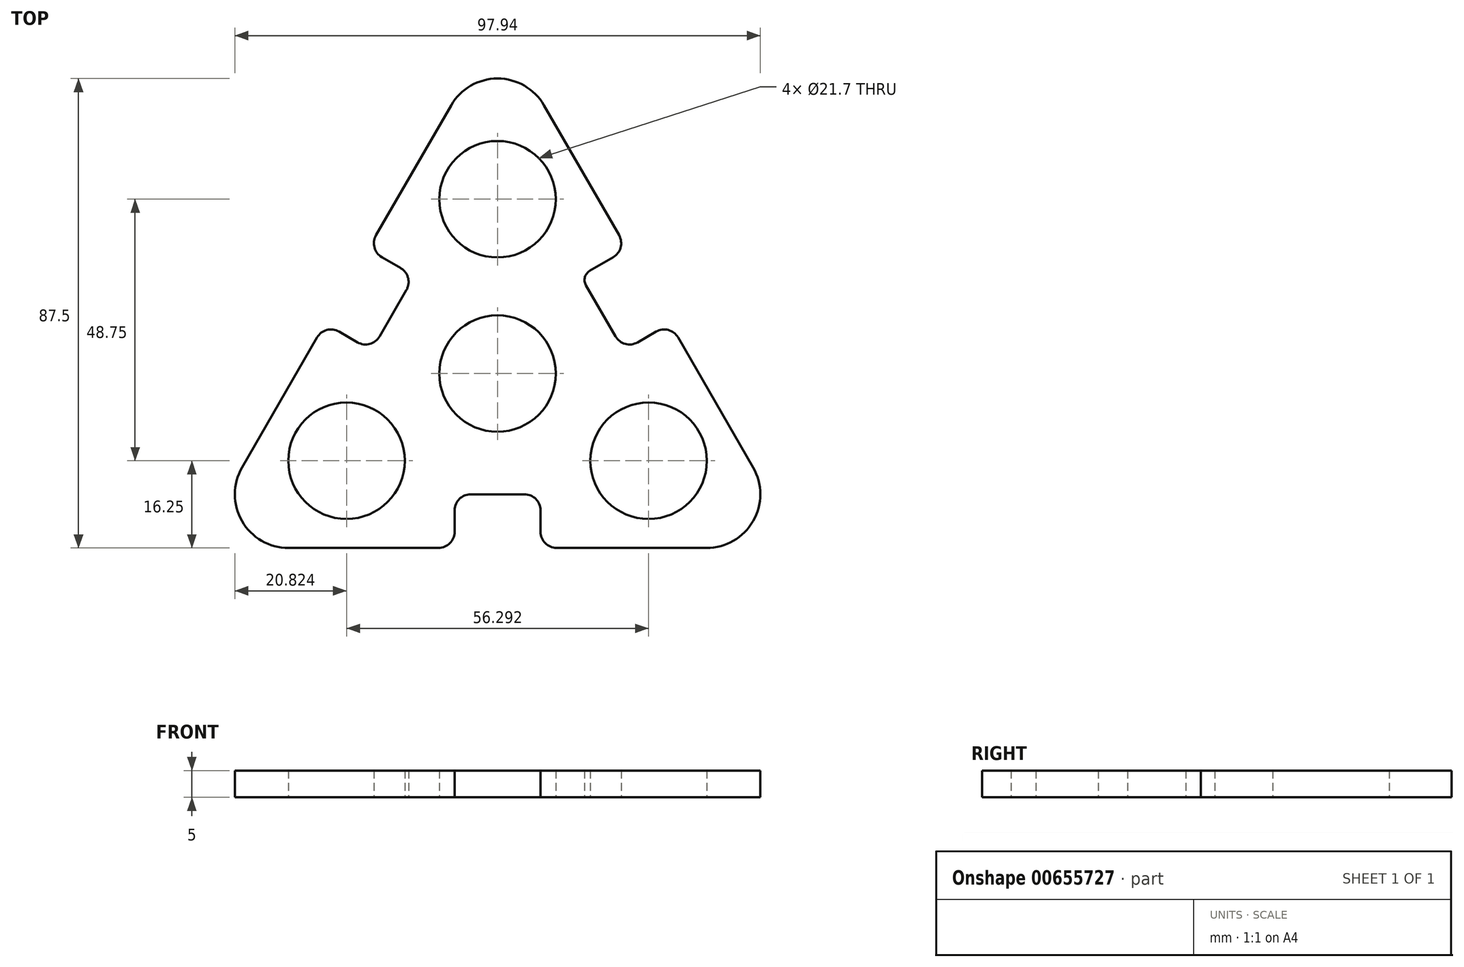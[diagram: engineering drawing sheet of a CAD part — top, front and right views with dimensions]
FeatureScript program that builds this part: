
annotation { "Feature Type Name" : "Feature", "Feature Type Description" : "" }
export const myFeature = defineFeature(function(context is Context, id is Id, definition is map)
    precondition{}
    {
        {
            var Q0;
            Q0=qCreatedBy(makeId("Top.planeOp"),FACE);
            var sketch = newSketch(context, id + "F0", { "sketchPlane" : qUnion([Q0])});
            skCircle(sketch, "E0.cCircle", {"center": v(0, 0) * mm, "radius": 32.5 * mm, "construction": true});
            skLineSegment(sketch, "E0.0", {"start": v(42.44, -32.5) * mm, "end": v(11, -32.5) * mm});
            skLineSegment(sketch, "E0.1", {"start": v(-56.3, -32.5) * mm, "end": v(0, 65) * mm, "construction": true});
            skLineSegment(sketch, "E0.2", {"start": v(0, 65) * mm, "end": v(56.3, -32.5) * mm, "construction": true});
            skPoint(sketch, "E0.0.midPoint", {"position": v(0, -32.5) * mm});
            skLineSegment(sketch, "E1.bottom", {"start": v(5, -22.5) * mm, "end": v(-5, -22.5) * mm});
            skLineSegment(sketch, "E1.left", {"start": v(8, -25.5) * mm, "end": v(8, -29.5) * mm});
            skLineSegment(sketch, "E1.right", {"start": v(-8, -25.5) * mm, "end": v(-8, -29.5) * mm});
            skLineSegment(sketch, "E2.trimOffspring", {"start": v(-11, -32.5) * mm, "end": v(-21.64, -32.5) * mm});
            skLineSegment(sketch, "E3", {"start": v(0, 0) * mm, "end": v(-28.15, -16.25) * mm, "construction": true});
            skCircle(sketch, "E4", {"center": v(-28.15, -16.25) * mm, "radius": 10.85 * mm});
            skCircle(sketch, "E5.1.0", {"center": v(28.15, -16.25) * mm, "radius": 10.85 * mm});
            skLineSegment(sketch, "E5.1.1", {"start": v(26.08, 5.82) * mm, "end": v(29.55, 7.82) * mm});
            skLineSegment(sketch, "E5.1.2", {"start": v(16.49, 16.45) * mm, "end": v(21.99, 6.92) * mm});
            skLineSegment(sketch, "E5.1.3", {"start": v(17.22, 19.18) * mm, "end": v(21.55, 21.68) * mm});
            skCircle(sketch, "E5.2.0", {"center": v(0, 32.5) * mm, "radius": 10.85 * mm});
            skLineSegment(sketch, "E5.2.1", {"start": v(-18.08, 19.68) * mm, "end": v(-21.55, 21.68) * mm});
            skLineSegment(sketch, "E5.2.2", {"start": v(-21.99, 6.92) * mm, "end": v(-16.99, 15.58) * mm});
            skLineSegment(sketch, "E5.2.3", {"start": v(-26.08, 5.82) * mm, "end": v(-29.55, 7.82) * mm});
            skLineSegment(sketch, "E6", {"start": v(22.65, 25.78) * mm, "end": v(4.76, 56.75) * mm});
            skLineSegment(sketch, "E7", {"start": v(-4.76, 56.75) * mm, "end": v(-22.65, 25.78) * mm});
            skLineSegment(sketch, "E8", {"start": v(-33.65, 6.72) * mm, "end": v(-51.53, -24.25) * mm});
            skLineSegment(sketch, "E9", {"start": v(51.53, -24.25) * mm, "end": v(33.65, 6.72) * mm});
            skPoint(sketch, "E10.visualSharp", {"position": v(-8, -32.5) * mm});
            skArc(sketch, "E10.filletArc", {"start": v(-11, -32.5) * mm, "mid": v(-8.88, -31.62) * mm, "end": v(-8, -29.5) * mm});
            skPoint(sketch, "E11.visualSharp", {"position": v(8, -32.5) * mm});
            skArc(sketch, "E11.filletArc", {"start": v(8, -29.5) * mm, "mid": v(8.88, -31.62) * mm, "end": v(11, -32.5) * mm});
            skPoint(sketch, "E12.visualSharp", {"position": v(-32.15, 9.32) * mm});
            skArc(sketch, "E12.filletArc", {"start": v(-29.55, 7.82) * mm, "mid": v(-31.82, 8.12) * mm, "end": v(-33.65, 6.72) * mm});
            skPoint(sketch, "E13.visualSharp", {"position": v(-24.15, 23.18) * mm});
            skArc(sketch, "E13.filletArc", {"start": v(-22.65, 25.78) * mm, "mid": v(-22.95, 23.5) * mm, "end": v(-21.55, 21.68) * mm});
            skPoint(sketch, "E14.visualSharp", {"position": v(-15.49, 18.18) * mm});
            skArc(sketch, "E14.filletArc", {"start": v(-16.99, 15.58) * mm, "mid": v(-16.69, 17.86) * mm, "end": v(-18.08, 19.68) * mm});
            skPoint(sketch, "E15.visualSharp", {"position": v(-23.49, 4.32) * mm});
            skArc(sketch, "E15.filletArc", {"start": v(-26.08, 5.82) * mm, "mid": v(-23.8, 5.52) * mm, "end": v(-21.99, 6.92) * mm});
            skPoint(sketch, "E16.visualSharp", {"position": v(15.49, 18.18) * mm});
            skArc(sketch, "E16.filletArc", {"start": v(17.22, 19.18) * mm, "mid": v(16.29, 17.96) * mm, "end": v(16.49, 16.45) * mm});
            skPoint(sketch, "E17.visualSharp", {"position": v(24.15, 23.18) * mm});
            skArc(sketch, "E17.filletArc", {"start": v(21.55, 21.68) * mm, "mid": v(22.95, 23.5) * mm, "end": v(22.65, 25.78) * mm});
            skPoint(sketch, "E18.visualSharp", {"position": v(23.49, 4.32) * mm});
            skArc(sketch, "E18.filletArc", {"start": v(21.99, 6.92) * mm, "mid": v(23.8, 5.52) * mm, "end": v(26.08, 5.82) * mm});
            skPoint(sketch, "E19.visualSharp", {"position": v(32.15, 9.32) * mm});
            skArc(sketch, "E19.filletArc", {"start": v(33.65, 6.72) * mm, "mid": v(31.82, 8.12) * mm, "end": v(29.55, 7.82) * mm});
            skPoint(sketch, "E20.visualSharp", {"position": v(8, -22.5) * mm});
            skArc(sketch, "E20.filletArc", {"start": v(8, -25.5) * mm, "mid": v(7.12, -23.38) * mm, "end": v(5, -22.5) * mm});
            skPoint(sketch, "E21.visualSharp", {"position": v(-8, -22.5) * mm});
            skArc(sketch, "E21.filletArc", {"start": v(-5, -22.5) * mm, "mid": v(-7.12, -23.38) * mm, "end": v(-8, -25.5) * mm});
            skPoint(sketch, "E22.visualSharp", {"position": v(56.3, -32.5) * mm});
            skPoint(sketch, "E23.visualSharp", {"position": v(0, 65) * mm});
            skPoint(sketch, "E24.visualSharp", {"position": v(-56.3, -32.5) * mm});
            skCircle(sketch, "E25", {"center": v(0, 0) * mm, "radius": 10.85 * mm});
            skLineSegment(sketch, "E26", {"start": v(-51.53, -24.25) * mm, "end": v(-56.3, -32.5) * mm});
            skLineSegment(sketch, "E27", {"start": v(-21.64, -32.5) * mm, "end": v(-56.3, -32.5) * mm});
            skLineSegment(sketch, "E28", {"start": v(56.3, -32.5) * mm, "end": v(42.44, -32.5) * mm});
            skLineSegment(sketch, "E29", {"start": v(56.3, -32.5) * mm, "end": v(51.53, -24.25) * mm});
            skLineSegment(sketch, "E30", {"start": v(0, 65) * mm, "end": v(-4.76, 56.75) * mm});
            skLineSegment(sketch, "E31", {"start": v(4.76, 56.75) * mm, "end": v(0, 65) * mm});
            skSolve(sketch);
        }
        {
            var Q0;
            Q0=makeQuery(id+"F0.imprint","IMPRINT",FACE,{"disambiguationData":[TD([[makeQuery(id+"F0.imprint","IMPRINT",EDGE,{"derivedFrom":sQuery(id+"F0.wireOp",EDGE,"E0.0")}),-1.0]])]});
            extrude(context, id + "F1", {"entities" : qUnion([Q0]), "depth" : 5 * mm, "offsetDistance" : 25 * mm});
        }
        {
            var Q0;
            Q0=makeQuery(id+"F1.opExtrude","SWEPT_EDGE",EDGE,{"disambiguationData":[OSD([sQuery(id+"F0.wireOp",EDGE,"E28"),sQuery(id+"F0.wireOp",EDGE,"E29")])]});
            var Q1;
            Q1=makeQuery(id+"F1.opExtrude","SWEPT_EDGE",EDGE,{"disambiguationData":[OSD([sQuery(id+"F0.wireOp",EDGE,"E30"),sQuery(id+"F0.wireOp",EDGE,"E31")])]});
            var Q2;
            Q2=makeQuery(id+"F1.opExtrude","SWEPT_EDGE",EDGE,{"disambiguationData":[OSD([sQuery(id+"F0.wireOp",EDGE,"E26"),sQuery(id+"F0.wireOp",EDGE,"E27")])]});
            fillet(context, id + "F2", {"entities" : qUnion([Q0, Q1, Q2]), "radius" : 10 * mm, "tangentPropagation" : true, "allowEdgeOverflow" : false});
        }
    });
